# Revit family: Mixer-Bath Shower-Caroma Titan1
name_source: partatom
category: Plumbing Fixtures
revit_build: Autodesk Revit 2013 (Build: 20121003_2115(x64)
units: mm (PartAtom-declared; Revit-internal decimal feet)

## types (1)
- Standard
    Assembly Code = C1030210
    CW Connection = Yes
    CWFU = 2
    Connector Radius = 10 mm  [stored 0.0328084 ft]
    Cost = 271.82 $
    Default Elevation = 900 mm  [stored 2.95276 ft]
    Description = Caroma Titan Bath Shower Mixer
    HW Connection = Yes
    HWFU = 2
    Manufacturer = GWA Bathrooms & Kitchens
    Material_ANZRS = Metal-Stainless Steel-Caroma
    Model = 99001SS
    ModifiedIssue_ANZRS = 2013.2 $
    Type Comments = 35mm Cartridge
    URL = http://www.caroma.com.au
    Vent Connection = No
    Waste Connection = No

note: [stored X ft] marks values corroborated as IEEE doubles in the binary element streams (Revit-internal decimal feet)

## geometry (parser evidence)
native form markers: Blend x16, Sweep x1
no freeform markers — native parametric forms only
